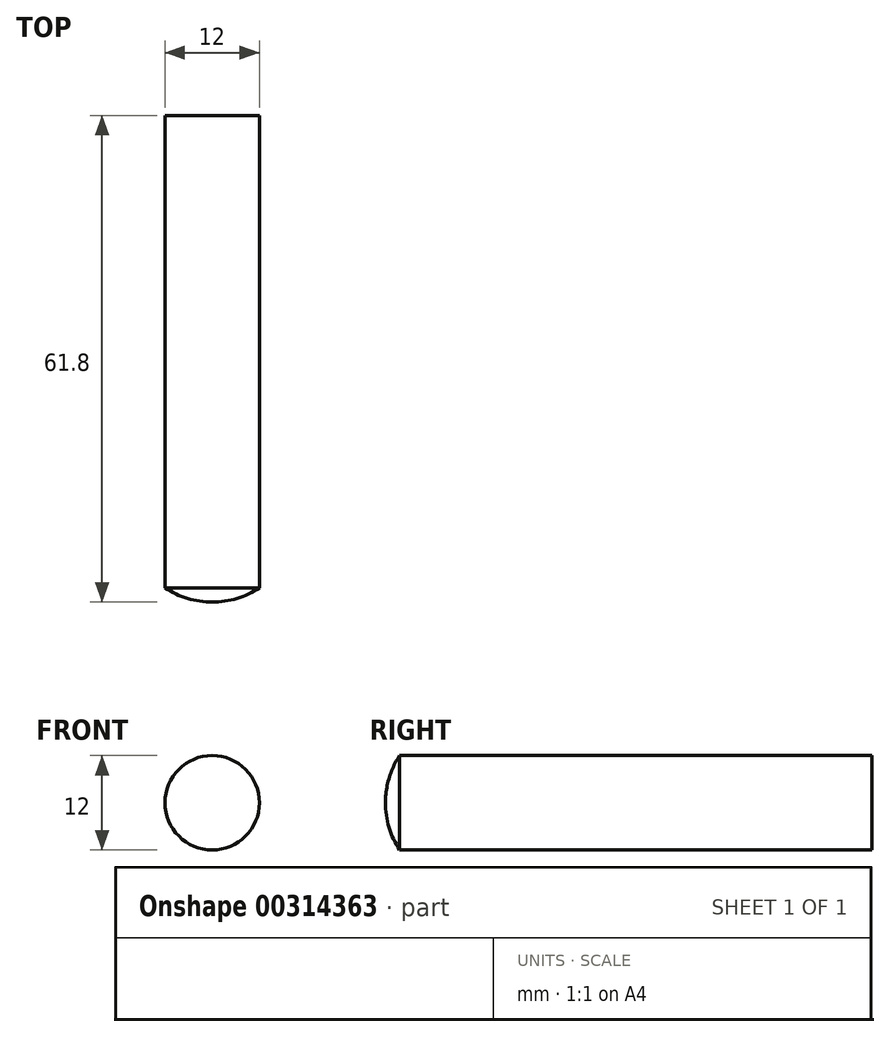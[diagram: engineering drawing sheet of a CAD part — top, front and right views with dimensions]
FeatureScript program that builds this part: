
annotation { "Feature Type Name" : "Feature", "Feature Type Description" : "" }
export const myFeature = defineFeature(function(context is Context, id is Id, definition is map)
    precondition{}
    {
        {
            var Q0;
            Q0=qCreatedBy(makeId("Front.planeOp"),FACE);
            var sketch = newSketch(context, id + "F0", { "sketchPlane" : qUnion([Q0])});
            skCircle(sketch, "E0", {"center": v(0, 0) * mm, "radius": 6 * mm});
            skSolve(sketch);
        }
        {
            var Q0;
            Q0=makeQuery(id+"F0.imprint","IMPRINT",FACE,{"disambiguationData":[TD([[makeQuery(id+"F0.imprint","IMPRINT",EDGE,{"derivedFrom":sQuery(id+"F0.wireOp",EDGE,"E0")}),1.0]])]});
            extrude(context, id + "F1", {"entities" : qUnion([Q0]), "depth" : 30 * mm, "hasSecondDirection" : true, "secondDirectionOppositeDirection" : true, "secondDirectionDepth" : 30 * mm});
        }
        {
            var Q0;
            Q0=qCreatedBy(makeId("Right.planeOp"),FACE);
            var sketch = newSketch(context, id + "F2", { "sketchPlane" : qUnion([Q0])});
            skLineSegment(sketch, "E1.0", {"start": v(-30, 0) * mm, "end": v(-30, 6) * mm});
            skArc(sketch, "E2", {"start": v(-30, 6) * mm, "mid": v(-31.34, 3.13) * mm, "end": v(-31.8, 0) * mm});
            skLineSegment(sketch, "E3", {"start": v(-30, 0) * mm, "end": v(-31.8, 0) * mm});
            skPoint(sketch, "E4.orphan", {"position": v(-30, -6) * mm});
            skSolve(sketch);
        }
        {
            var Q0;
            Q0=makeQuery(id+"F2.imprint","IMPRINT",FACE,{"disambiguationData":[TD([[makeQuery(id+"F2.imprint","IMPRINT",EDGE,{"derivedFrom":sQuery(id+"F2.wireOp",EDGE,"E1.0")}),1.0]])]});
            var Q1;
            Q1=makeQuery(id+"F1.opExtrude","SWEPT_FACE",FACE,{"disambiguationData":[OSD([sQuery(id+"F0.wireOp",EDGE,"E0")])]});
            revolve(context, id + "F3", {"operationType" : NewBodyOperationType.ADD, "entities" : qUnion([Q0]), "axis" : qUnion([Q1]), "revolveType" : RevolveType.FULL});
        }
    });
